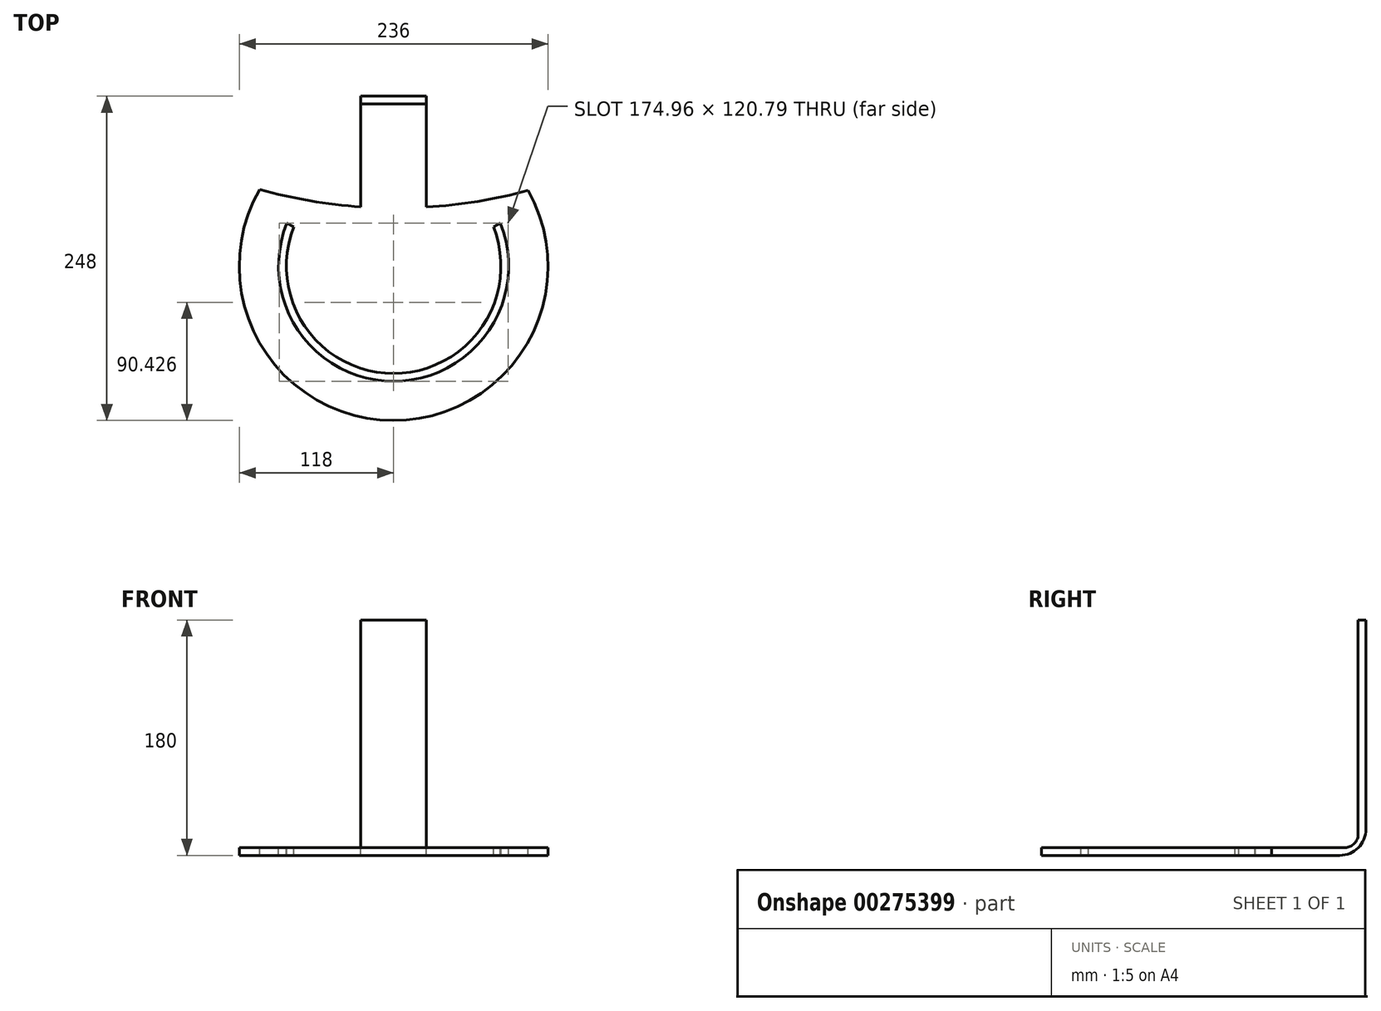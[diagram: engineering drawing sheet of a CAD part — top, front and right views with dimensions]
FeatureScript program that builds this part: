
annotation { "Feature Type Name" : "Feature", "Feature Type Description" : "" }
export const myFeature = defineFeature(function(context is Context, id is Id, definition is map)
    precondition{}
    {
        {
            var Q0;
            Q0=qCreatedBy(makeId("Front.planeOp"),FACE);
            var sketch = newSketch(context, id + "F0", { "sketchPlane" : qUnion([Q0])});
            skLineSegment(sketch, "E0.bottom", {"start": v(-30, 30) * mm, "end": v(20, 30) * mm});
            skLineSegment(sketch, "E0.top", {"start": v(-30, -70) * mm, "end": v(20, -70) * mm});
            skLineSegment(sketch, "E0.left", {"start": v(-30, 30) * mm, "end": v(-30, -70) * mm});
            skLineSegment(sketch, "E0.right", {"start": v(20, 30) * mm, "end": v(20, -70) * mm});
            skLineSegment(sketch, "E1.top", {"start": v(-30, -150) * mm, "end": v(20, -150) * mm});
            skLineSegment(sketch, "E1.left", {"start": v(-30, -70) * mm, "end": v(-30, -150) * mm});
            skLineSegment(sketch, "E1.right", {"start": v(20, -70) * mm, "end": v(20, -150) * mm});
            skLineSegment(sketch, "E2.top", {"start": v(-30, -144) * mm, "end": v(20, -144) * mm});
            skLineSegment(sketch, "E2.left", {"start": v(-30, -150) * mm, "end": v(-30, -144) * mm});
            skLineSegment(sketch, "E2.right", {"start": v(20, -150) * mm, "end": v(20, -144) * mm});
            skSolve(sketch);
        }
        {
            var Q0;
            Q0=makeQuery(id+"F0.imprint","IMPRINT",FACE,{"disambiguationData":[TD([[makeQuery(id+"F0.imprint","IMPRINT",EDGE,{"derivedFrom":sQuery(id+"F0.wireOp",EDGE,"E1.top")}),1.0]])]});
            var sketch = newSketch(context, id + "F1", { "sketchPlane" : qUnion([Q0])});
            skSolve(sketch);
        }
        {
            var Q0;
            Q0 = qSketchRegion(id + "F1", true);
            var Q1;
            Q1=makeQuery(id+"F0.imprint","IMPRINT",FACE,{"disambiguationData":[TD([[makeQuery(id+"F0.imprint","IMPRINT",EDGE,{"derivedFrom":sQuery(id+"F0.wireOp",EDGE,"E1.top")}),1.0]])]});
            extrude(context, id + "F2", {"entities" : qUnion([Q0, Q1]), "depth" : 130 * mm});
        }
        {
            var Q0;
            Q0 = qSketchRegion(id + "F0", true);
            extrude(context, id + "F3", {"entities" : qUnion([Q0]), "operationType" : NewBodyOperationType.ADD, "depth" : 6 * mm, "offsetDistance" : 25 * mm});
        }
        {
            var Q0;
            Q0=makeQuery(id+"F2.opExtrude","CAP_EDGE",EDGE,{"disambiguationData":[OSD([sQuery(id+"F0.wireOp",EDGE,"E1.top")])],"isStart":true});
            fillet(context, id + "F4", {"entities" : qUnion([Q0]), "radius" : 20 * mm, "tangentPropagation" : true, "allowEdgeOverflow" : false});
        }
        {
            var Q0;
            Q0=makeQuery(id+"F3.boolean.opBoolean","INTERSECT",EDGE,{"derivedFrom":[makeQuery(id+"F2.opExtrude","SWEPT_FACE",FACE,{"disambiguationData":[OSD([sQuery(id+"F0.wireOp",EDGE,"E2.top")])]}),makeQuery(id+"F3.opExtrude","CAP_FACE",FACE,{"disambiguationData":[OSD([sQuery(id+"F0.wireOp",EDGE,"E0.bottom"),sQuery(id+"F0.wireOp",EDGE,"E0.left"),sQuery(id+"F0.wireOp",EDGE,"E0.right"),sQuery(id+"F0.wireOp",EDGE,"E1.left"),sQuery(id+"F0.wireOp",EDGE,"E1.right"),sQuery(id+"F0.wireOp",EDGE,"E1.top"),sQuery(id+"F0.wireOp",EDGE,"E2.left"),sQuery(id+"F0.wireOp",EDGE,"E2.right")])],"isStart":false})]});
            fillet(context, id + "F5", {"entities" : qUnion([Q0]), "radius" : 10 * mm, "tangentPropagation" : true, "allowEdgeOverflow" : false});
        }
        {
            var Q0;
            Q0=makeQuery(id+"F2.opExtrude","SWEPT_FACE",FACE,{"disambiguationData":[OSD([sQuery(id+"F0.wireOp",EDGE,"E2.top")])]});
            var sketch = newSketch(context, id + "F6", { "sketchPlane" : qUnion([Q0])});
            skArc(sketch, "E3", {"start": v(-107.42, -71.4) * mm, "mid": v(-5.41, -248) * mm, "end": v(97.82, -72.1) * mm});
            skArc(sketch, "E4", {"start": v(-107.42, -71.4) * mm, "mid": v(-4.84, -85.52) * mm, "end": v(97.82, -72.1) * mm});
            skSolve(sketch);
        }
        {
            var Q0;
            {var subQ3=sQuery(id+"F6.wireOp",EDGE,"E3");Q0=makeQuery(id+"F6.imprint","IMPRINT",FACE,{"disambiguationData":[TD([[makeQuery(id+"F6.imprint","IMPRINT",EDGE,{"derivedFrom":subQ3}),1.0]])]});}
            extrude(context, id + "F7", {"entities" : qUnion([Q0]), "operationType" : NewBodyOperationType.ADD, "oppositeDirection" : true, "depth" : 6 * mm, "offsetDistance" : 25 * mm});
        }
        {
            var Q0;
            {var subQ0=sQuery(id+"F0.wireOp",EDGE,"E2.top");Q0=makeQuery(id+"F7.boolean.opBoolean","MERGE",FACE,{"derivedFrom":[makeQuery(id+"F2.opExtrude","SWEPT_FACE",FACE,{"disambiguationData":[OSD([subQ0])]}),makeQuery(id+"F7.opExtrude","CAP_FACE",FACE,{"disambiguationData":[OSD([sQuery(id+"F0.wireOp",EDGE,"E1.left"),sQuery(id+"F0.wireOp",EDGE,"E1.right"),subQ0,sQuery(id+"F0.wireOp",EDGE,"E2.left"),sQuery(id+"F0.wireOp",EDGE,"E2.right"),sQuery(id+"F6.wireOp",EDGE,"E3"),sQuery(id+"F6.wireOp",EDGE,"E4")])],"isStart":true})]});}
            var sketch = newSketch(context, id + "F8", { "sketchPlane" : qUnion([Q0])});
            skPoint(sketch, "E5.centerSnap0", {"position": v(-5, -16) * mm});
            skArc(sketch, "E6", {"start": v(-86.62, -97.18) * mm, "mid": v(-77.9, -179.25) * mm, "end": v(-5, -217.97) * mm});
            skArc(sketch, "E7", {"start": v(-81.29, -99.93) * mm, "mid": v(-72.78, -176.14) * mm, "end": v(-5, -212) * mm});
            skLineSegment(sketch, "E8", {"start": v(-5, -130) * mm, "end": v(-5, -286.78) * mm, "construction": true});
            skLineSegment(sketch, "E9", {"start": v(-5, -286.78) * mm, "end": v(-5, -130) * mm, "construction": true});
            skLineSegment(sketch, "E10", {"start": v(0, 71.96) * mm, "end": v(-5, 73.8) * mm, "construction": true});
            skLineSegment(sketch, "E11", {"start": v(-5, 73.8) * mm, "end": v(-5, -130) * mm, "construction": true});
            skLineSegment(sketch, "E12.trimOffspring", {"start": v(-86.62, -97.18) * mm, "end": v(-81.29, -99.93) * mm});
            skLineSegment(sketch, "E13.MirrorCS", {"start": v(76.62, -97.18) * mm, "end": v(71.29, -99.93) * mm});
            skArc(sketch, "E14.MirrorCS", {"start": v(71.29, -99.93) * mm, "mid": v(62.78, -176.14) * mm, "end": v(-5, -212) * mm});
            skArc(sketch, "E15.MirrorCS", {"start": v(76.62, -97.18) * mm, "mid": v(67.9, -179.25) * mm, "end": v(-5, -217.97) * mm});
            skSolve(sketch);
        }
        {
            var Q0;
            Q0=makeQuery(id+"F8.imprint","IMPRINT",FACE,{"disambiguationData":[TD([[makeQuery(id+"F8.imprint","IMPRINT",EDGE,{"derivedFrom":sQuery(id+"F8.wireOp",EDGE,"E5")}),-1.0]])]});
            var Q1;
            Q1=makeQuery(id+"F8.imprint","IMPRINT",FACE,{"disambiguationData":[TD([[makeQuery(id+"F8.imprint","IMPRINT",EDGE,{"derivedFrom":sQuery(id+"F8.wireOp",EDGE,"E6")}),1.0]])]});
            extrude(context, id + "F9", {"entities" : qUnion([Q0, Q1]), "operationType" : NewBodyOperationType.REMOVE, "oppositeDirection" : true, "depth" : 31 * mm, "offsetDistance" : 25 * mm});
        }
    });
